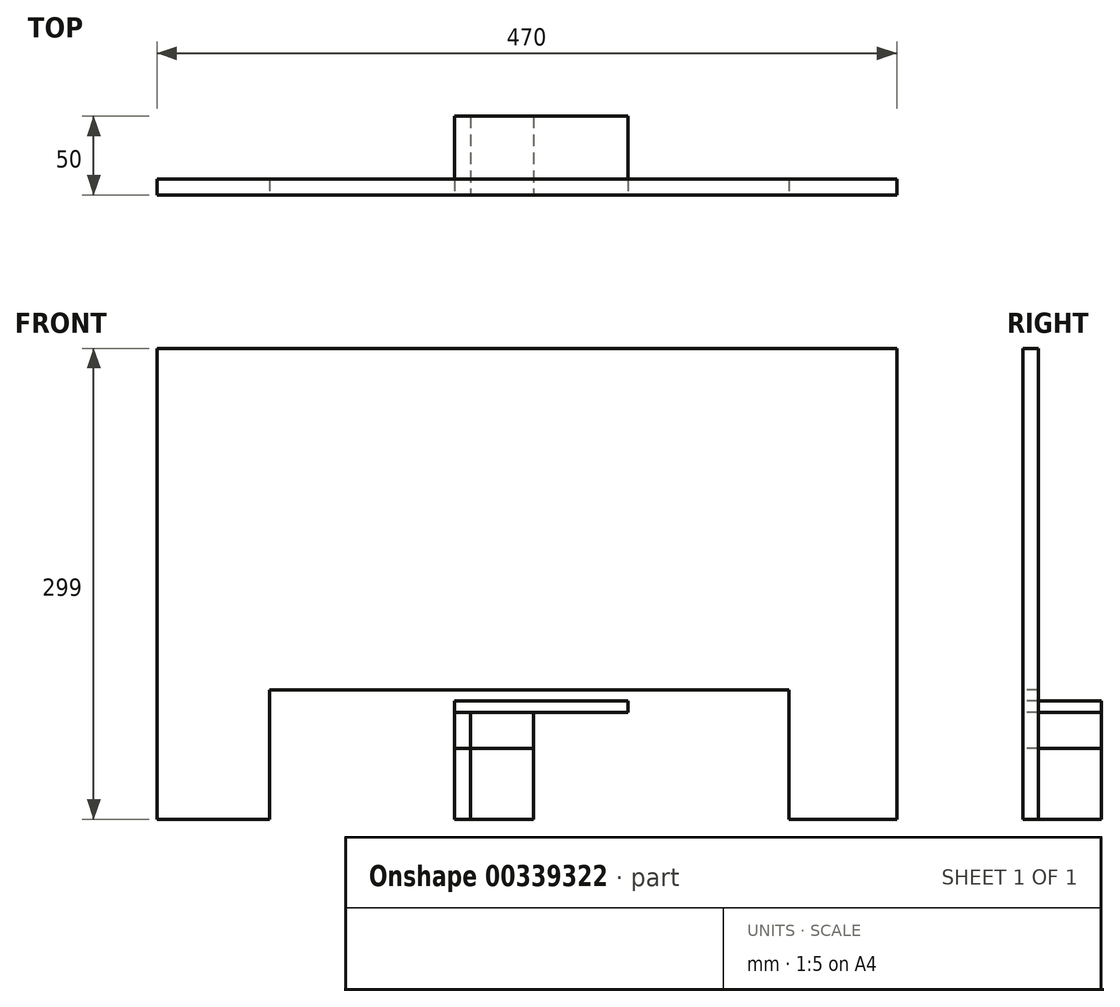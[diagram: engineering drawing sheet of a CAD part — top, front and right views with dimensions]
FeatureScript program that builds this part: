
annotation { "Feature Type Name" : "Feature", "Feature Type Description" : "" }
export const myFeature = defineFeature(function(context is Context, id is Id, definition is map)
    precondition{}
    {
        {
            var Q0;
            Q0=qCreatedBy(makeId("Front.planeOp"),FACE);
            var sketch = newSketch(context, id + "F0", { "sketchPlane" : qUnion([Q0])});
            skLineSegment(sketch, "E0.bottom", {"start": v(-74.23, 0) * mm, "end": v(395.77, 0) * mm});
            skLineSegment(sketch, "E0.top", {"start": v(-74.23, 299) * mm, "end": v(395.77, 299) * mm});
            skLineSegment(sketch, "E0.left", {"start": v(-74.23, 0) * mm, "end": v(-74.23, 299) * mm});
            skLineSegment(sketch, "E0.right", {"start": v(395.77, 0) * mm, "end": v(395.77, 299) * mm});
            skLineSegment(sketch, "E1", {"start": v(114.97, 0) * mm, "end": v(114.97, 45) * mm});
            skLineSegment(sketch, "E2", {"start": v(114.97, 45) * mm, "end": v(124.97, 45) * mm});
            skLineSegment(sketch, "E3", {"start": v(124.97, 45) * mm, "end": v(124.97, 0) * mm});
            skLineSegment(sketch, "E4", {"start": v(124.97, 45) * mm, "end": v(124.97, 68) * mm});
            skLineSegment(sketch, "E5", {"start": v(124.97, 68) * mm, "end": v(114.97, 68) * mm});
            skLineSegment(sketch, "E6", {"start": v(114.97, 75) * mm, "end": v(224.97, 75) * mm});
            skLineSegment(sketch, "E7", {"start": v(224.97, 75) * mm, "end": v(224.97, 68) * mm});
            skLineSegment(sketch, "E8", {"start": v(224.97, 68) * mm, "end": v(124.97, 68) * mm});
            skLineSegment(sketch, "E9", {"start": v(-2.75, 82) * mm, "end": v(-2.75, 0) * mm});
            skLineSegment(sketch, "E10", {"start": v(114.97, 45) * mm, "end": v(114.97, 68) * mm});
            skLineSegment(sketch, "E11", {"start": v(114.97, 68) * mm, "end": v(114.97, 75) * mm});
            skLineSegment(sketch, "E12", {"start": v(124.97, 45) * mm, "end": v(164.97, 45) * mm});
            skLineSegment(sketch, "E13", {"start": v(164.97, 45) * mm, "end": v(164.97, 0) * mm});
            skLineSegment(sketch, "E14", {"start": v(164.97, 45) * mm, "end": v(164.97, 68) * mm});
            skLineSegment(sketch, "E15", {"start": v(-2.75, 82) * mm, "end": v(327.25, 82) * mm});
            skLineSegment(sketch, "E16", {"start": v(327.25, 82) * mm, "end": v(327.25, 0) * mm});
            skSolve(sketch);
        }
        {
            assignVariable(context, id + "F1", {"name" : "Depth", "anyValue" : 50});
        }
        {
            var Q0;
            Q0=makeQuery(id+"F0.imprint","IMPRINT",FACE,{"disambiguationData":[TD([[makeQuery(id+"F0.imprint","IMPRINT",EDGE,{"derivedFrom":sQuery(id+"F0.wireOp",EDGE,"E0.top")}),-1.0]])]});
            extrude(context, id + "F2", {"entities" : qUnion([Q0]), "oppositeDirection" : true, "depth" : 10 * mm});
        }
        {
            var Q0;
            {var subQ0=sQuery(id+"F0.wireOp",EDGE,"E3");Q0=makeQuery(id+"F0.imprint","IMPRINT",FACE,{"disambiguationData":[TD([[makeQuery(id+"F0.imprint","IMPRINT",EDGE,{"derivedFrom":subQ0}),1.0]])]});}
            extrude(context, id + "F3", {"entities" : qUnion([Q0]), "oppositeDirection" : true, "depth" : (getVariable(context, 'Depth')) * mm});
        }
        {
            var Q0;
            {var subQ3=sQuery(id+"F0.wireOp",EDGE,"E5");Q0=makeQuery(id+"F0.imprint","IMPRINT",FACE,{"disambiguationData":[TD([[makeQuery(id+"F0.imprint","IMPRINT",EDGE,{"derivedFrom":subQ3}),-1.0]])]});}
            extrude(context, id + "F4", {"entities" : qUnion([Q0]), "oppositeDirection" : true, "depth" : (getVariable(context, 'Depth')) * mm});
        }
        {
            var Q0;
            {var subQ0=sQuery(id+"F0.wireOp",EDGE,"E1");Q0=makeQuery(id+"F0.imprint","IMPRINT",FACE,{"disambiguationData":[TD([[makeQuery(id+"F0.imprint","IMPRINT",EDGE,{"derivedFrom":subQ0}),-1.0]])]});}
            extrude(context, id + "F5", {"entities" : qUnion([Q0]), "oppositeDirection" : true, "depth" : (getVariable(context, 'Depth')) * mm});
        }
        {
            var Q0;
            {var subQ0=sQuery(id+"F0.wireOp",EDGE,"E4");Q0=makeQuery(id+"F0.imprint","IMPRINT",FACE,{"disambiguationData":[TD([[makeQuery(id+"F0.imprint","IMPRINT",EDGE,{"derivedFrom":subQ0}),-1.0]])]});}
            extrude(context, id + "F6", {"entities" : qUnion([Q0]), "oppositeDirection" : true, "depth" : (getVariable(context, 'Depth')) * mm});
        }
        {
            var Q0;
            Q0=makeQuery(id+"F0.imprint","IMPRINT",FACE,{"disambiguationData":[TD([[makeQuery(id+"F0.imprint","IMPRINT",EDGE,{"derivedFrom":sQuery(id+"F0.wireOp",EDGE,"E2")}),1.0]])]});
            extrude(context, id + "F7", {"entities" : qUnion([Q0]), "oppositeDirection" : true, "depth" : (getVariable(context, 'Depth')) * mm});
        }
    });
